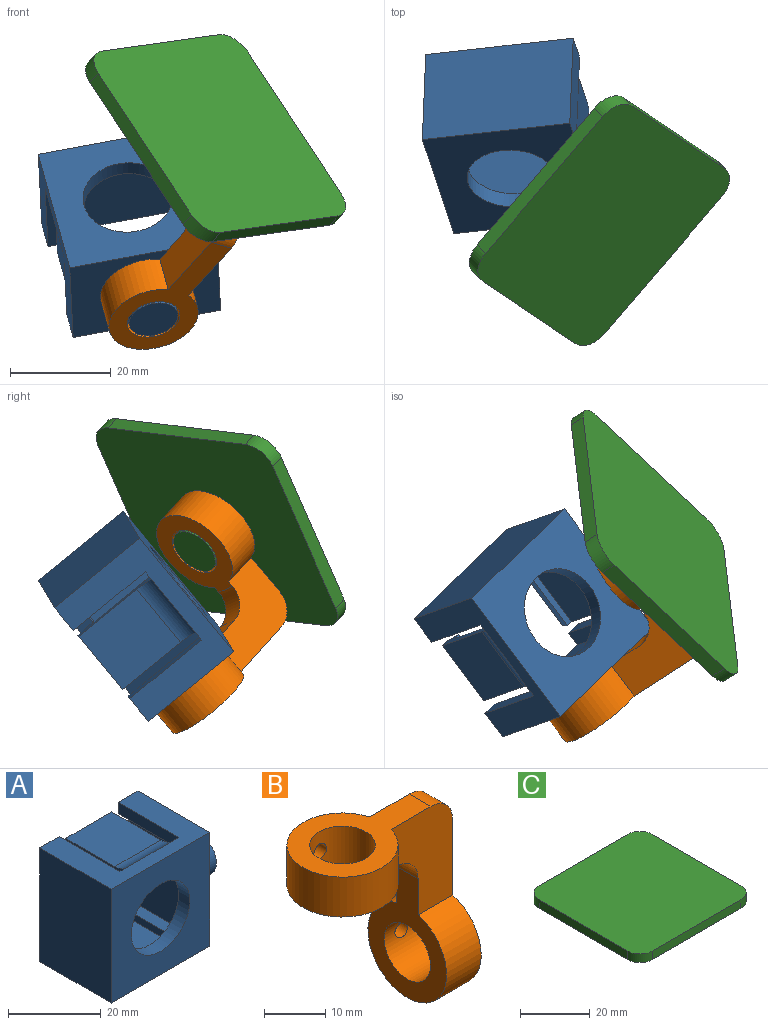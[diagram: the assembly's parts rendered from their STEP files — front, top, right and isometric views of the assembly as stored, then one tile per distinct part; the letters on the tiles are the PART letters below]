
ASSEMBLY  parts=3 mates=2
PART A: 37 faces, bbox 38x21.9x30 mm
  f0: plane 18.48x3mm, normal (0,0,-1), area 55.4mm2, adj f4,f5,f6,f34
  f1: plane 18.48x3mm, normal (0,0,1), area 55.4mm2, adj f4,f8,f23,f33
  f2: plane 15.08x14mm, normal (0,0,-1), area 211.1mm2, adj f4,f11,f13,f15
  f3: plane 18.48x3mm, normal (0,0,-1), area 55.4mm2, adj f4,f8,f9,f33
  f4: plane 30.02x24mm, normal (0,1,0), area 351.6mm2, adj f0,f1,f2,f3,f5,f9,f10,f11
  f5: plane 18.48x3mm, normal (1,0,0), area 55.4mm2, adj f0,f4,f6,f10
  f6: plane 30.02x6mm, normal (0,1,0), area 108.1mm2, adj f0,f5,f10,f18,f21,f22,f24,f34
  f7: plane 30.02x30mm, normal (0,-1,0), area 651.8mm2, adj f10,f18,f19,f24,f32
  f8: plane 30.02x6mm, normal (0,1,0), area 108.1mm2, adj f1,f3,f9,f10,f19,f23,f24,f33
  f9: plane 18.48x3mm, normal (-1,0,0), area 55.4mm2, adj f3,f4,f8,f10
  f10: plane 30x21.88mm, normal (0,0,1), area 323.8mm2, adj f4,f5,f6,f7,f8,f9,f17,f18
  f11: plane 18.48x4.17mm, normal (1,0,0), area 31.4mm2, adj f2,f4,f12,f14,f15,f16,f17
  f12: plane 14x1.51mm, normal (0,1,0), area 21.1mm2, adj f11,f13,f14,f16
  f13: plane 18.48x4.17mm, normal (-1,0,0), area 31.4mm2, adj f2,f4,f12,f14,f15,f16,f17
  f14: plane 14.91x14mm, normal (0,0,1), area 208.7mm2, adj f11,f12,f13,f17
  f15: plane 14x1.17mm, normal (0,-0.98,-0.17), area 16.7mm2, adj f2,f11,f13,f16
  f16: plane 14x3.19mm, normal (0,0.34,-0.94), area 47.6mm2, adj f11,f12,f13,f15
  f17: cylinder r=5mm len=14mm, axis (-1,0,0), area 55.7mm2, adj f10,f11,f13,f14
  f18: plane 30.02x21.88mm, normal (-1,0,0), area 656.8mm2, adj f6,f7,f10,f24
  f19: plane 30.02x21.88mm, normal (1,0,0), area 579.4mm2, adj f7,f8,f10,f24,f35
  f20: plane 15.08x14mm, normal (0,0,1), area 211.1mm2, adj f4,f25,f27,f29
  f21: plane 18.48x3mm, normal (0,0,1), area 55.4mm2, adj f4,f6,f22,f34
  f22: plane 18.48x3mm, normal (1,0,0), area 55.4mm2, adj f4,f6,f21,f24
  f23: plane 18.48x3mm, normal (-1,0,0), area 55.4mm2, adj f1,f4,f8,f24
  f24: plane 30x21.88mm, normal (0,0,-1), area 323.8mm2, adj f4,f6,f7,f8,f18,f19,f22,f23
  f25: plane 18.48x4.17mm, normal (1,0,0), area 31.4mm2, adj f4,f20,f26,f28,f29,f30,f31
  f26: plane 14x1.51mm, normal (0,1,0), area 21.1mm2, adj f25,f27,f28,f30
  f27: plane 18.48x4.17mm, normal (-1,0,0), area 31.4mm2, adj f4,f20,f26,f28,f29,f30,f31
  f28: plane 14.91x14mm, normal (0,0,-1), area 208.7mm2, adj f25,f26,f27,f31
  f29: plane 14x1.17mm, normal (0,-0.98,0.17), area 16.7mm2, adj f20,f25,f27,f30
  f30: plane 14x3.19mm, normal (0,0.34,0.94), area 47.6mm2, adj f25,f26,f27,f29
  f31: cylinder r=5mm len=14mm, axis (-1,0,0), area 55.7mm2, adj f24,f25,f27,f28
  f32: cylinder r=8.9mm len=17.8mm, axis (0,1,0), area 190.1mm2, adj f4,f7
  f33: plane 24.02x18.48mm, normal (-1,0,0), area 443.9mm2, adj f1,f3,f4,f8
  f34: plane 24.02x18.48mm, normal (1,0,0), area 443.9mm2, adj f0,f4,f6,f21
  f35: cylinder r=4.96mm len=9.93mm, axis (-1,0,0), area 249.5mm2, adj f19,f36
  f36: plane 9.93x9.93mm, normal (1,0,0), area 77.4mm2, adj f35
PART B: 14 faces, bbox 32.1x18.2x38.1 mm
  f0: cylinder r=5.36mm len=10.73mm, axis (0,0,-1), area 262.4mm2, adj f2,f3,f13
  f1: cylinder r=9.1mm len=18.2mm, axis (0,0,-1), area 409.7mm2, adj f2,f3,f4,f5,f13
  f2: plane 27.09x18.2mm, normal (0,0,1), area 214.8mm2, adj f0,f1,f4,f5,f9
  f3: plane 19.09x18.2mm, normal (0,0,-1), area 174.8mm2, adj f0,f1,f4,f5,f8
  f4: plane 20.24x14.24mm, normal (0,-1,0), area 211.8mm2, adj f1,f2,f3,f6,f7,f8,f9,f11
  f5: plane 20.24x14.24mm, normal (0,1,0), area 211.8mm2, adj f1,f2,f3,f6,f7,f8,f9,f11
  f6: plane 25.09x18.2mm, normal (-1,0,0), area 204.8mm2, adj f4,f5,f8,f10,f11
  f7: plane 33.09x18.2mm, normal (1,0,0), area 244.8mm2, adj f4,f5,f9,f10,f11
  f8: cylinder r=5mm len=5mm, axis (0,-1,0), area 39.3mm2, adj f3,f4,f5,f6
  f9: cylinder r=5mm len=5mm, axis (0,1,0), area 39.3mm2, adj f2,f4,f5,f7
  f10: cylinder r=5.36mm len=10.73mm, axis (-1,0,0), area 262.4mm2, adj f6,f7,f12
  f11: cylinder r=9.1mm len=18.2mm, axis (-1,0,0), area 409.8mm2, adj f4,f5,f6,f7,f12
  f12: cylinder r=1.5mm len=3.95mm, axis (0,-1,0), area 35.6mm2, adj f10,f11
  f13: cylinder r=1.5mm len=3.95mm, axis (0,-1,0), area 35.6mm2, adj f0,f1
PART C: 12 faces, bbox 46x46x11 mm
  f0: cylinder r=4.97mm len=9.95mm, axis (0,0,1), area 250mm2, adj f1,f7
  f1: plane 9.95x9.95mm, normal (0,0,-1), area 77.7mm2, adj f0
  f2: plane 36x3mm, normal (0,-1,0), area 108mm2, adj f6,f7,f8,f11
  f3: plane 36x3mm, normal (1,0,0), area 108mm2, adj f6,f7,f8,f9
  f4: plane 36x3mm, normal (0,1,0), area 108mm2, adj f6,f7,f9,f10
  f5: plane 36x3mm, normal (-1,0,0), area 108mm2, adj f6,f7,f10,f11
  f6: plane 46x46mm, normal (0,0,1), area 2094.5mm2, adj f2,f3,f4,f5,f8,f9,f10,f11
  f7: plane 46x46mm, normal (0,0,-1), area 2016.8mm2, adj f0,f2,f3,f4,f5,f8,f9,f10
  f8: cylinder r=5mm len=5mm, axis (0,0,-1), area 23.6mm2, adj f2,f3,f6,f7
  f9: cylinder r=5mm len=5mm, axis (0,0,1), area 23.6mm2, adj f3,f4,f6,f7
  f10: cylinder r=5mm len=5mm, axis (0,0,-1), area 23.6mm2, adj f4,f5,f6,f7
  f11: cylinder r=5mm len=5mm, axis (0,0,1), area 23.6mm2, adj f2,f5,f6,f7
PLACE A rot(axis=(-0.37,0.87,-0.33),85.3deg) t=(22.33,19.06,1.74)mm
PLACE B rot(axis=(0.16,0.67,-0.72),79.2deg) t=(22.33,19.06,1.74)mm
PLACE C rot(axis=(0.36,0.75,-0.55),63.7deg) t=(22.33,19.05,1.73)mm fixed
MATE revolute C.f0 <-> B.f0  axis (-0.56,0.55,-0.61) through (34.12,7.41,14.62)mm
MATE revolute B.f10 <-> A.f35  axis (0.21,-0.62,-0.75) through (27.12,4.72,-15.6)mm
